# Revit family: 634-00-001 DN300
name_source: partatom
category: Pipe Accessories
units: mm (PartAtom-declared; Revit-internal decimal feet)

## family parameters
Always vertical = Yes
Cut with Voids When Loaded = No
Part Type = Valve - Breaks Into
Round Connector Dimension = Use Diameter
Shared = No
Work Plane-Based = No

## types (2) — shared parameters
10 = 10 mm  [stored 0.0328084 ft]
2 = 2 mm  [stored 0.00656168 ft]
Bolt_L = 65 mm  [stored 0.213255 ft]
Bore = 150 mm  [stored 0.492126 ft]
D = 273 mm
D-10 = 263 mm
D1 = 193 mm  [stored 0.633202 ft]
D11 = 218 mm  [stored 0.715223 ft]
D12 = 17 mm
D1_L = 102 mm  [stored 0.334646 ft]
D2 = 41 mm  [stored 0.134514 ft]
D2_L = 81 mm  [stored 0.265748 ft]
DN = 300 mm  [stored 0.984252 ft]
DN300_PN16_AVK ref. no. 634-356-00-016 = 634-356-00-016
DN300_PN16_AVK ref. no. 634-356-00-036 = 634-356-00-036
Description_ = AVK SUPA MAXI™ END CAP, PN16
FL_T = 25 mm  [stored 0.082021 ft]
L = 150 mm  [stored 0.492126 ft]
L-L1 = 41 mm  [stored 0.134514 ft]
L1 = 75 mm
Nut = 16 mm
Radius = 43 mm  [stored 0.141076 ft]
S1 = 157 mm  [stored 0.515092 ft]
S2 = 178 mm  [stored 0.58399 ft]
Search_table = 634-00-001 DN300
URL product pages = https://www.avkvalves.com
zero-valued in all types: Default Elevation, Thickness

## type names (no varying parameters)
- DN300_PN16_AVK ref. no. 634-356-00-016
- DN300_PN16_AVK ref. no. 634-356-00-036

note: [stored X ft] marks values corroborated as IEEE doubles in the binary element streams (Revit-internal decimal feet)

## geometry (parser evidence)
native form markers: Sweep x3
no freeform markers — native parametric forms only
